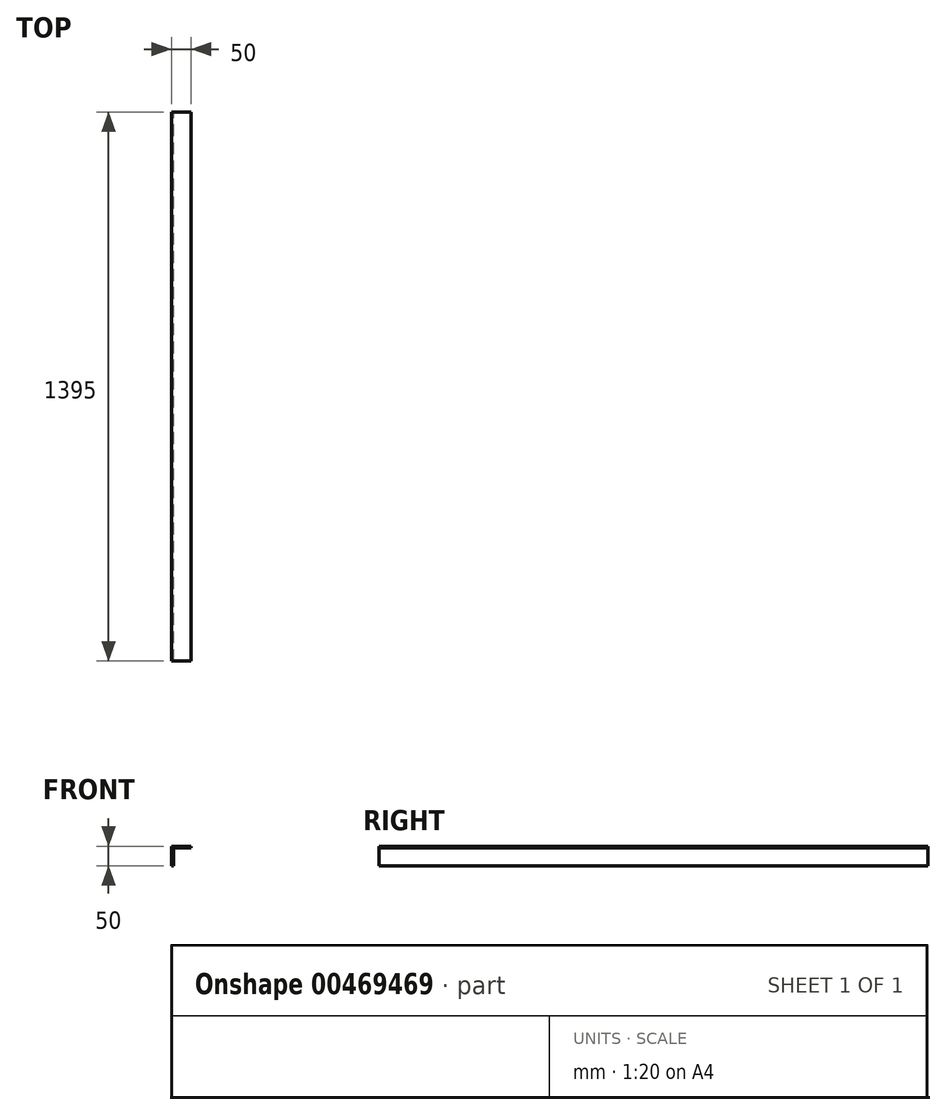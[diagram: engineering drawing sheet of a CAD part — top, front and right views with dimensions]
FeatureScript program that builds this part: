
annotation { "Feature Type Name" : "Feature", "Feature Type Description" : "" }
export const myFeature = defineFeature(function(context is Context, id is Id, definition is map)
    precondition{}
    {
        {
            var Q0;
            Q0=qCreatedBy(makeId("Front.planeOp"),FACE);
            var sketch = newSketch(context, id + "F0", { "sketchPlane" : qUnion([Q0])});
            skLineSegment(sketch, "E0", {"start": v(0, 0) * mm, "end": v(0, 50) * mm});
            skLineSegment(sketch, "E1", {"start": v(0, 50) * mm, "end": v(50, 50) * mm});
            skLineSegment(sketch, "E2", {"start": v(50, 50) * mm, "end": v(50, 45) * mm});
            skLineSegment(sketch, "E3", {"start": v(50, 45) * mm, "end": v(5, 45) * mm});
            skLineSegment(sketch, "E4", {"start": v(5, 45) * mm, "end": v(5, 0) * mm});
            skLineSegment(sketch, "E5", {"start": v(5, 0) * mm, "end": v(0, 0) * mm});
            skSolve(sketch);
        }
        {
            var Q0;
            Q0 = qSketchRegion(id + "F0", true);
            extrude(context, id + "F1", {"entities" : qUnion([Q0]), "depth" : 1395 * mm});
        }
    });
